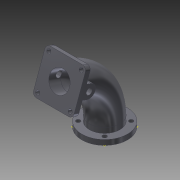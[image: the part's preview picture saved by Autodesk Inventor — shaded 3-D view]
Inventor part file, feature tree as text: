
AUTODESK INVENTOR PART (.ipt)
format: ipt  version: 2011 SP2 (Build 150309200, 309)  size: 260,608 bytes
history: native  units: mm
features: hole x6, sketch x6, extrude x3, fillet x3, sweep x1, plane x1, shell x1, mirror x1, projected_geometry x1
ambient origin geometry x8: Origin, YZ Plane, XZ Plane, XY Plane, X Axis, Y Axis, Z Axis, Center Point
bodies: Solid1 (feature_tree)
feature tree (23):
  sweep  "Sweep1"
  plane  "Work Plane1"
  extrude  "Extrusion1"  Depth=12.217305mm
  extrude  "Extrusion2"  [1 undecoded]
  fillet  "Fillet1"  Radius=45.0mm
  shell  "Shell1"  Thickness=10.0mm
  extrude  "Extrusion3"  Depth=10.0mm TaperAngle=0.0deg
  mirror  "Mirror1"
  fillet  "Fillet2"  Radius=8.0mm
  fillet  "Fillet3"  Radius=10.0mm
  hole  "Hole1"  [1 undecoded]
  hole  "Hole2"  [1 undecoded]
  hole  "Hole3"  [1 undecoded]
  hole  "Hole4"  [1 undecoded]
  hole  "Hole5"  [1 undecoded]
  hole  "Hole6"  [1 undecoded]
  sketch  "Sketch1"  dims[d0=30.0mm d1=25.0mm]
  sketch  "Sketch2"  dims[d2=100.0mm d3=12.217305mm]
  sketch  "Sketch3"  dims[d4=0.0mm d5=-5.0mm d6=45.0mm d7=10.0mm d8=0.0mm]
  sketch  "Sketch4"  dims[d10=80.0mm d11=10.0mm d12=0.0mm d13=8.0mm d14=10.0mm]
  sketch  "Sketch5"  dims[d15=25.0mm d16=22.5mm]
  projected_geometry  "Projected Loop1"
  sketch  "Sketch6"  dims[d17=10.0mm d18=0.0mm d19=10.0mm d20=10.0mm d21=12.0mm d22=6.0mm d23=4.0mm d24=2.0mm d25=90.0deg d26=8.0mm d27=0.0mm d28=10.0mm d29=10.0mm d30=8.0mm d31=6.0mm d32=4.0mm d33=2.0mm d34=90.0deg d35=10.0mm d36=0.0mm d37=10.0mm d38=10.0mm d39=8.0mm d40=6.0mm d41=4.0mm d42=2.0mm d43=90.0deg d44=10.0mm d45=0.0mm d46=10.0mm d47=10.0mm d48=8.0mm d49=6.0mm d50=4.0mm d51=2.0mm d52=90.0deg d53=10.0mm d54=0.0mm d55=10.0mm d56=10.0mm d57=8.0mm d58=6.0mm d59=4.0mm d60=2.0mm d61=90.0deg d62=10.0mm d63=0.0mm d64=37.0mm d65=45.0deg d66=40.0mm d68=360.0deg d70=8.0mm d71=6.0mm d72=4.0mm d73=2.0mm d74=90.0deg d75=10.0mm d76=20.594885mm]
note: 7 required parameter values undecoded (feature->parameter linkage not recoverable at this tier; creation-order binding heuristic only, values carry confidence <= 0.55)
